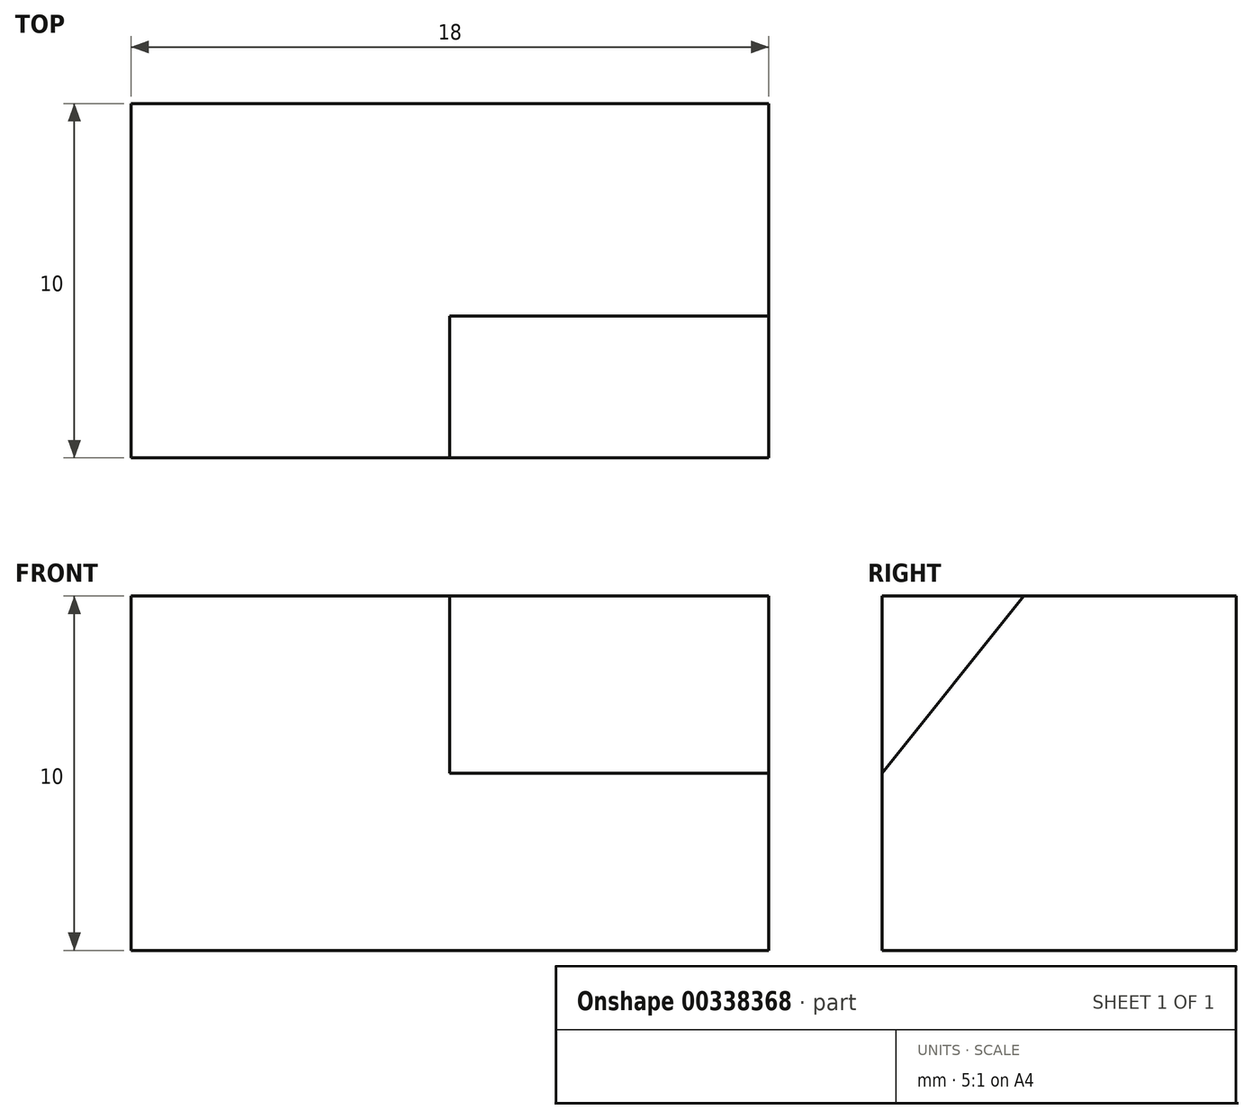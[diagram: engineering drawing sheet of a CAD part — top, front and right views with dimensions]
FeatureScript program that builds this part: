
annotation { "Feature Type Name" : "Feature", "Feature Type Description" : "" }
export const myFeature = defineFeature(function(context is Context, id is Id, definition is map)
    precondition{}
    {
        {
            var Q0;
            Q0=qCreatedBy(makeId("Top.planeOp"),FACE);
            var sketch = newSketch(context, id + "F0", { "sketchPlane" : qUnion([Q0])});
            skLineSegment(sketch, "E0.bottom", {"start": v(0, 0) * mm, "end": v(18, 0) * mm});
            skLineSegment(sketch, "E0.top", {"start": v(0, -10) * mm, "end": v(18, -10) * mm});
            skLineSegment(sketch, "E0.left", {"start": v(0, 0) * mm, "end": v(0, -10) * mm});
            skLineSegment(sketch, "E0.right", {"start": v(18, 0) * mm, "end": v(18, -10) * mm});
            skSolve(sketch);
        }
        {
            var Q0;
            Q0 = qSketchRegion(id + "F0", true);
            extrude(context, id + "F1", {"entities" : qUnion([Q0]), "depth" : 10 * mm});
        }
        {
            var Q0;
            Q0=makeQuery(id+"F1.opExtrude","SWEPT_FACE",FACE,{"disambiguationData":[OSD([sQuery(id+"F0.wireOp",EDGE,"E0.right")])]});
            var sketch = newSketch(context, id + "F2", { "sketchPlane" : qUnion([Q0])});
            skLineSegment(sketch, "E1", {"start": v(-10, 5) * mm, "end": v(-10, 10) * mm});
            skLineSegment(sketch, "E2", {"start": v(-10, 10) * mm, "end": v(-6, 10) * mm});
            skLineSegment(sketch, "E3", {"start": v(-6, 10) * mm, "end": v(-10, 5) * mm});
            skSolve(sketch);
        }
        {
            var Q0;
            Q0 = qSketchRegion(id + "F2", true);
            extrude(context, id + "F3", {"entities" : qUnion([Q0]), "operationType" : NewBodyOperationType.REMOVE, "oppositeDirection" : true, "depth" : 9 * mm});
        }
    });
